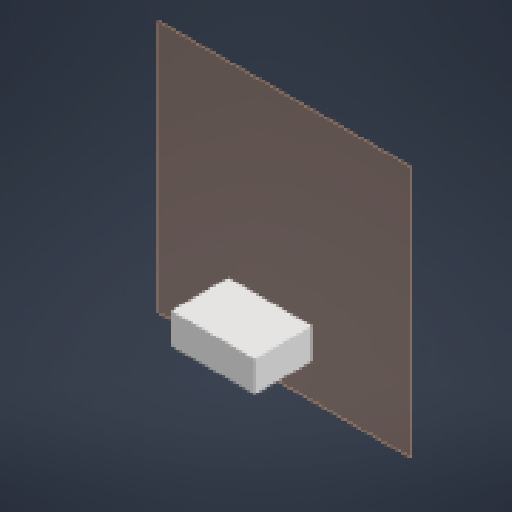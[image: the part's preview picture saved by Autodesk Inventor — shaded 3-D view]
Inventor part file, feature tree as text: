
AUTODESK INVENTOR PART (.ipt)
format: ipt  version: 2024 (Build 280153000, 153)  size: 135,168 bytes
history: native  units: mm
features: other x4, sketch x3, plane x1, extrude x1
ambient origin geometry x8: Origin, YZ Plane, XZ Plane, XY Plane, X Axis, Y Axis, Z Axis, Center Point
bodies: Body1 (feature_tree)
feature tree (9):
  other  "Sólido1"
  plane  "Plano de trabajo1"
  extrude  "Extrusión1"  Depth=800.0mm
  sketch  "Boceto2"  dims[d2=400.0mm]
  sketch  "Boceto3"  dims[d3=400.0mm d4=1150.0mm d5=0.0mm d7=2190.0mm d8=1095.0mm d9=850.0mm d11=300.0mm d12=1150.0mm d13=2190.0mm d14=300.0mm d15=1095.0mm]
  sketch  "Boceto1"  dims[d0=2190.0mm d1=800.0mm]
  other  "<userpath>\Downloads\Celda_Robotizada.iam"
  other  "Celda_Robotizada.iam"
  other  "Piso:1"
